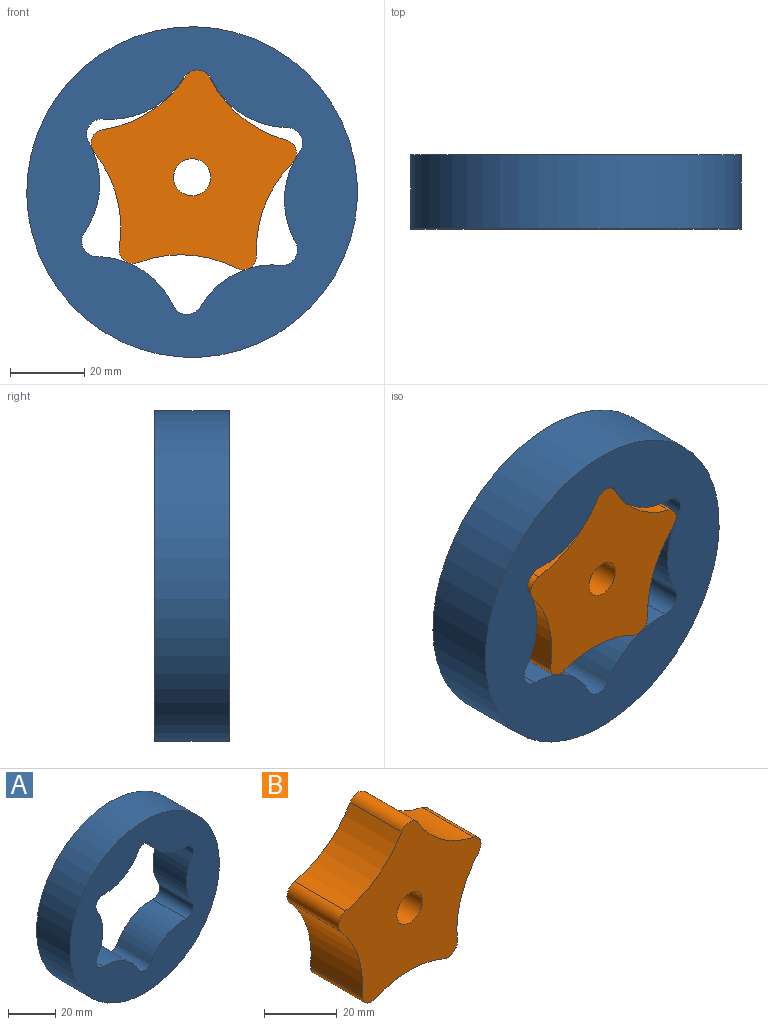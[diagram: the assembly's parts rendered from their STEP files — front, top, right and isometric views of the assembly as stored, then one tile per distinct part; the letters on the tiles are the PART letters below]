
ASSEMBLY  parts=2 mates=1
PART A: 15 faces, bbox 89.3x20x89.3 mm
  f0: cylinder r=4.14mm len=20mm, axis (0,1,0), area 179.9mm2, adj f1,f11,f13,f14
  f1: cylinder r=22.95mm len=21.19mm, axis (0,1,0), area 516.2mm2, adj f0,f2,f13,f14
  f2: cylinder r=4.14mm len=20mm, axis (0,1,0), area 179.9mm2, adj f1,f3,f13,f14
  f3: cylinder r=22.95mm len=24.47mm, axis (0,1,0), area 516.2mm2, adj f2,f4,f13,f14
  f4: cylinder r=4.14mm len=20mm, axis (0,1,0), area 179.9mm2, adj f3,f5,f13,f14
  f5: cylinder r=22.95mm len=21.19mm, axis (0,1,0), area 516.2mm2, adj f4,f6,f13,f14
  f6: cylinder r=4.14mm len=20mm, axis (0,1,0), area 179.9mm2, adj f5,f7,f13,f14
  f7: cylinder r=22.95mm len=21.19mm, axis (0,1,0), area 516.2mm2, adj f6,f8,f13,f14
  f8: cylinder r=4.14mm len=20mm, axis (0,1,0), area 179.9mm2, adj f7,f9,f13,f14
  f9: cylinder r=22.95mm len=24.47mm, axis (0,1,0), area 516.2mm2, adj f8,f10,f13,f14
  f10: cylinder r=4.14mm len=20mm, axis (0,1,0), area 179.9mm2, adj f9,f11,f13,f14
  f11: cylinder r=22.95mm len=21.19mm, axis (0,1,0), area 516.2mm2, adj f0,f10,f13,f14
  f12: cylinder r=44.63mm len=89.27mm, axis (0,1,0), area 5608.7mm2, adj f13,f14
  f13: plane 89.27x89.27mm, normal (0,-1,0), area 3769mm2, adj f0,f1,f2,f3,f4,f5,f6,f7
  f14: plane 89.27x89.27mm, normal (0,1,0), area 3769mm2, adj f0,f1,f2,f3,f4,f5,f6,f7
PART B: 13 faces, bbox 55.5x20x53.2 mm
  f0: cylinder r=3.67mm len=20mm, axis (0,1,0), area 153.7mm2, adj f1,f10,f11,f12
  f1: cylinder r=32.96mm len=26.79mm, axis (0,1,0), area 551.9mm2, adj f0,f2,f11,f12
  f2: cylinder r=3.67mm len=20mm, axis (0,1,0), area 153.7mm2, adj f1,f3,f11,f12
  f3: cylinder r=32.96mm len=25.48mm, axis (0,1,0), area 551.9mm2, adj f2,f4,f11,f12
  f4: cylinder r=3.67mm len=20mm, axis (0,1,0), area 153.7mm2, adj f3,f5,f11,f12
  f5: cylinder r=32.96mm len=21.68mm, axis (0,1,0), area 551.9mm2, adj f4,f6,f11,f12
  f6: cylinder r=3.67mm len=20mm, axis (0,1,0), area 153.7mm2, adj f5,f7,f11,f12
  f7: cylinder r=32.96mm len=21.68mm, axis (0,1,0), area 551.9mm2, adj f6,f8,f11,f12
  f8: cylinder r=3.67mm len=20mm, axis (0,1,0), area 153.7mm2, adj f7,f10,f11,f12
  f9: cylinder r=5mm len=20mm, axis (0,1,0), area 628.3mm2, adj f11,f12
  f10: cylinder r=32.96mm len=25.48mm, axis (0,1,0), area 551.9mm2, adj f0,f8,f11,f12
  f11: plane 55.52x53.16mm, normal (0,-1,0), area 1735.3mm2, adj f0,f1,f2,f3,f4,f5,f6,f7
  f12: plane 55.52x53.16mm, normal (0,1,0), area 1735.3mm2, adj f0,f1,f2,f3,f4,f5,f6,f7
PLACE A rot(axis=(0,1,0),122.7deg) t=(3.37,20,-2.16)mm
PLACE B rot(axis=(0,1,0),147.2deg) t=(0,20,4)mm
MATE planar B.f9 <-> A.f12  axis (0,1,0) through (0,0,4)mm
